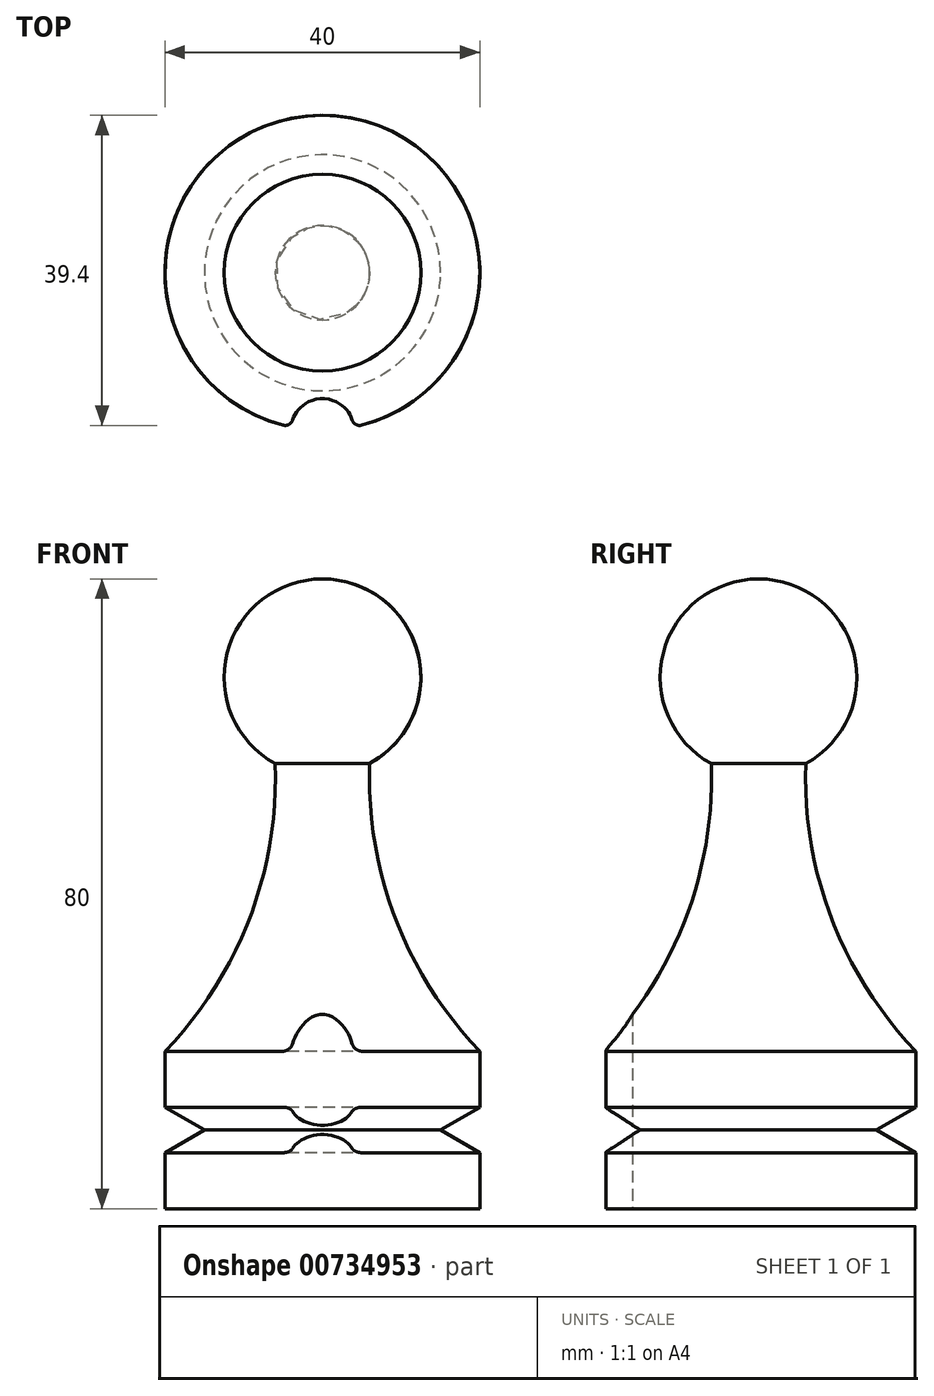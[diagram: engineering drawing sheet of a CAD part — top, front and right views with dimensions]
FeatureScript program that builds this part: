
annotation { "Feature Type Name" : "Feature", "Feature Type Description" : "" }
export const myFeature = defineFeature(function(context is Context, id is Id, definition is map)
    precondition{}
    {
        {
            var Q0;
            Q0=qCreatedBy(makeId("Front.planeOp"),FACE);
            var sketch = newSketch(context, id + "F0", { "sketchPlane" : qUnion([Q0])});
            skLineSegment(sketch, "E0", {"start": v(0, 98.28) * mm, "end": v(0, -65.56) * mm, "construction": true});
            skLineSegment(sketch, "E1", {"start": v(0, 0) * mm, "end": v(20, 0) * mm});
            skLineSegment(sketch, "E2", {"start": v(20, 0) * mm, "end": v(20, 7.11) * mm});
            skLineSegment(sketch, "E3", {"start": v(15, 10) * mm, "end": v(20, 7.11) * mm});
            skLineSegment(sketch, "E4", {"start": v(20, 12.89) * mm, "end": v(15, 10) * mm});
            skLineSegment(sketch, "E5", {"start": v(20, 12.89) * mm, "end": v(20, 20) * mm});
            skArc(sketch, "E6", {"start": v(6, 56.53) * mm, "mid": v(9.28, 36.84) * mm, "end": v(20, 20) * mm});
            skArc(sketch, "E7", {"start": v(6, 56.53) * mm, "mid": v(12.11, 70.6) * mm, "end": v(0, 80) * mm});
            skLineSegment(sketch, "E8", {"start": v(0, 80) * mm, "end": v(0, 0) * mm});
            skSolve(sketch);
        }
        {
            var Q0;
            Q0=makeQuery(id+"F0.imprint","IMPRINT",FACE,{"disambiguationData":[TD([[makeQuery(id+"F0.imprint","IMPRINT",EDGE,{"derivedFrom":sQuery(id+"F0.wireOp",EDGE,"E1")}),1.0]])]});
            var Q1;
            Q1=sQuery(id+"F0.wireOp",EDGE,"E0");
            revolve(context, id + "F1", {"surfaceOperationType" : NewSurfaceOperationType.NEW, "entities" : qUnion([Q0]), "axis" : qUnion([Q1]), "revolveType" : RevolveType.FULL});
        }
        {
            var Q0;
            Q0=qCreatedBy(makeId("Top.planeOp"),FACE);
            var sketch = newSketch(context, id + "F2", { "sketchPlane" : qUnion([Q0])});
            skCircle(sketch, "E9", {"center": v(0, -20) * mm, "radius": 4 * mm});
            skSolve(sketch);
        }
        {
            var Q0;
            Q0 = qSketchRegion(id + "F2", true);
            extrude(context, id + "F3", {"entities" : qUnion([Q0]), "operationType" : NewBodyOperationType.REMOVE, "depth" : 36.3 * mm, "offsetDistance" : 25 * mm});
        }
        {
            var Q0;
            Q0=makeQuery(id+"F3.boolean.opBoolean","INTERSECT",EDGE,{"disambiguationData":[OD(0.0)],"derivedFrom":[makeQuery(id+"F1.opRevolve","SWEPT_FACE",FACE,{"disambiguationData":[OSD([sQuery(id+"F0.wireOp",EDGE,"E5")])]}),makeQuery(id+"F3.opExtrude","SWEPT_FACE",FACE,{"disambiguationData":[OSD([sQuery(id+"F2.wireOp",EDGE,"E9")])]})]});
            var Q1;
            Q1=makeQuery(id+"F3.boolean.opBoolean","INTERSECT",EDGE,{"disambiguationData":[OD(0.0)],"derivedFrom":[makeQuery(id+"F1.opRevolve","SWEPT_FACE",FACE,{"disambiguationData":[OSD([sQuery(id+"F0.wireOp",EDGE,"E2")])]}),makeQuery(id+"F3.opExtrude","SWEPT_FACE",FACE,{"disambiguationData":[OSD([sQuery(id+"F2.wireOp",EDGE,"E9")])]})]});
            var Q2;
            Q2=makeQuery(id+"F3.boolean.opBoolean","INTERSECT",EDGE,{"disambiguationData":[OD(1.0)],"derivedFrom":[makeQuery(id+"F1.opRevolve","SWEPT_FACE",FACE,{"disambiguationData":[OSD([sQuery(id+"F0.wireOp",EDGE,"E2")])]}),makeQuery(id+"F3.opExtrude","SWEPT_FACE",FACE,{"disambiguationData":[OSD([sQuery(id+"F2.wireOp",EDGE,"E9")])]})]});
            var Q3;
            Q3=makeQuery(id+"F3.boolean.opBoolean","INTERSECT",EDGE,{"disambiguationData":[OD(1.0)],"derivedFrom":[makeQuery(id+"F1.opRevolve","SWEPT_FACE",FACE,{"disambiguationData":[OSD([sQuery(id+"F0.wireOp",EDGE,"E5")])]}),makeQuery(id+"F3.opExtrude","SWEPT_FACE",FACE,{"disambiguationData":[OSD([sQuery(id+"F2.wireOp",EDGE,"E9")])]})]});
            fillet(context, id + "F4", {"entities" : qUnion([Q0, Q1, Q2, Q3]), "radius" : 1 * mm, "tangentPropagation" : true, "allowEdgeOverflow" : false});
        }
    });
